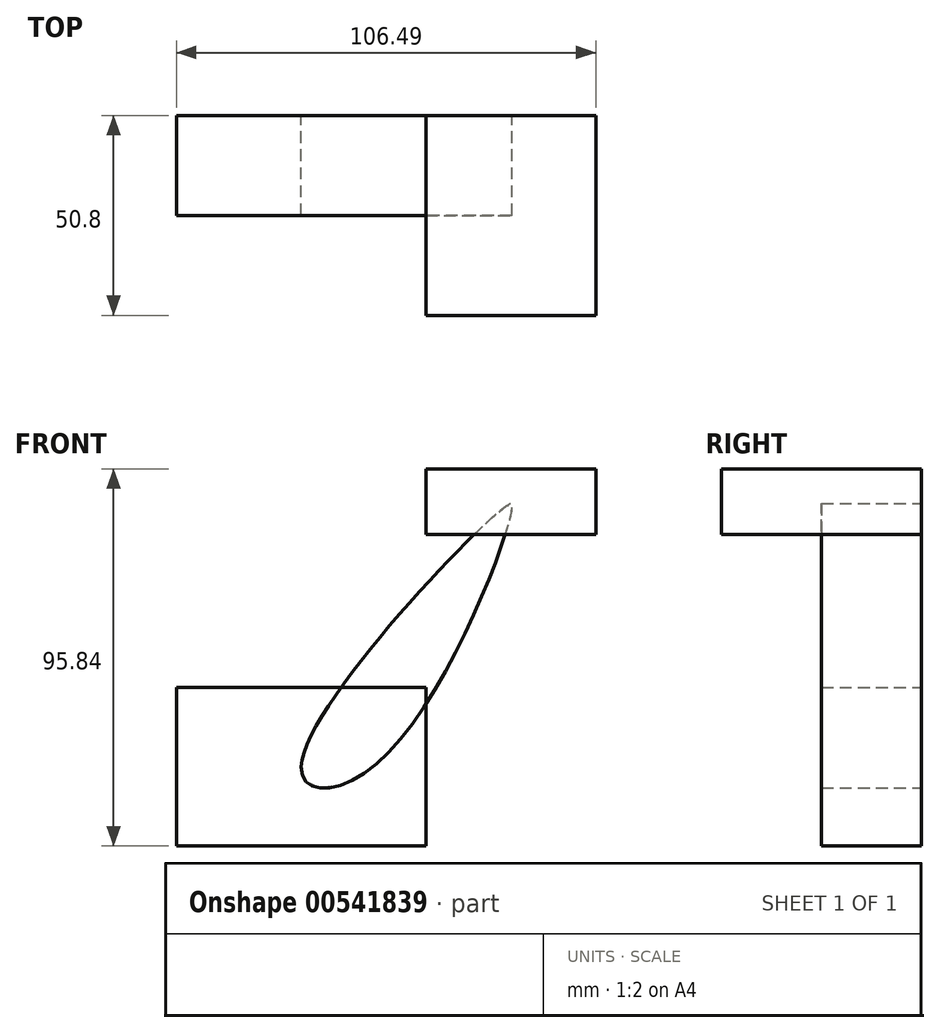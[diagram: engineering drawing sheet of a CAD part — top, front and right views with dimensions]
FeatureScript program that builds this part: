
annotation { "Feature Type Name" : "Feature", "Feature Type Description" : "" }
export const myFeature = defineFeature(function(context is Context, id is Id, definition is map)
    precondition{}
    {
        {
            var Q0;
            Q0=qCreatedBy(makeId("Front.planeOp"),FACE);
            var sketch = newSketch(context, id + "F0", { "sketchPlane" : qUnion([Q0])});
            skLineSegment(sketch, "E0.bottom", {"start": v(31.66, -20.15) * mm, "end": v(-31.66, -20.15) * mm});
            skLineSegment(sketch, "E0.top", {"start": v(31.66, 20.15) * mm, "end": v(-31.66, 20.15) * mm});
            skLineSegment(sketch, "E0.left", {"start": v(31.66, -20.15) * mm, "end": v(31.66, 20.15) * mm});
            skLineSegment(sketch, "E0.right", {"start": v(-31.66, -20.15) * mm, "end": v(-31.66, 20.15) * mm});
            skPoint(sketch, "E0.middle", {"position": v(0, 0) * mm});
            skLineSegment(sketch, "E1.bottom", {"start": v(31.66, 59) * mm, "end": v(74.83, 59) * mm});
            skLineSegment(sketch, "E1.top", {"start": v(31.66, 75.7) * mm, "end": v(74.83, 75.7) * mm});
            skLineSegment(sketch, "E1.left", {"start": v(31.66, 59) * mm, "end": v(31.66, 75.7) * mm});
            skLineSegment(sketch, "E1.right", {"start": v(74.83, 59) * mm, "end": v(74.83, 75.7) * mm});
            skPoint(sketch, "E1.middle", {"position": v(53.24, 67.35) * mm});
            skLineSegment(sketch, "E2", {"start": v(0, 20.15) * mm, "end": v(0, 67.63) * mm});
            skPoint(sketch, "E2.endSnap0", {"position": v(0, 20.15) * mm});
            skSolve(sketch);
        }
        {
            var Q0;
            Q0=makeQuery(id+"F0.imprint","IMPRINT",FACE,{"disambiguationData":[TD([[makeQuery(id+"F0.imprint","IMPRINT",EDGE,{"derivedFrom":sQuery(id+"F0.wireOp",EDGE,"E0.bottom")}),-1.0]])]});
            var Q1;
            Q1=makeQuery(id+"F0.imprint","IMPRINT",FACE,{"disambiguationData":[TD([[makeQuery(id+"F0.imprint","IMPRINT",EDGE,{"derivedFrom":sQuery(id+"F0.wireOp",EDGE,"E1.bottom")}),1.0]])]});
            extrude(context, id + "F1", {"entities" : qUnion([Q0, Q1]), "depth" : 25.4 * mm, "offsetDistance" : 25.4 * mm});
        }
        {
            var Q0;
            Q0=makeQuery(id+"F1.opExtrude","CAP_FACE",FACE,{"disambiguationData":[OSD([sQuery(id+"F0.wireOp",EDGE,"E1.bottom"),sQuery(id+"F0.wireOp",EDGE,"E1.top"),sQuery(id+"F0.wireOp",EDGE,"E1.left"),sQuery(id+"F0.wireOp",EDGE,"E1.right")])],"isStart":false});
            extrude(context, id + "F2", {"entities" : qUnion([Q0]), "operationType" : NewBodyOperationType.ADD, "depth" : 25.4 * mm, "offsetDistance" : 25.4 * mm});
        }
        {
            var Q0;
            Q0=qCreatedBy(makeId("Front.planeOp"),FACE);
            var sketch = newSketch(context, id + "F3", { "sketchPlane" : qUnion([Q0])});
            skFitSpline(sketch, "E3", {"points": [v(0, 0) * mm, v(52.52, 66.6) * mm, v(53.55, 66.26) * mm, v(18.3, 0) * mm, v(0, 0) * mm]});
            skSolve(sketch);
        }
        {
            var Q0;
            Q0 = qSketchRegion(id + "F3", true);
            extrude(context, id + "F4", {"entities" : qUnion([Q0]), "depth" : 25.4 * mm, "offsetDistance" : 25.4 * mm});
        }
    });
